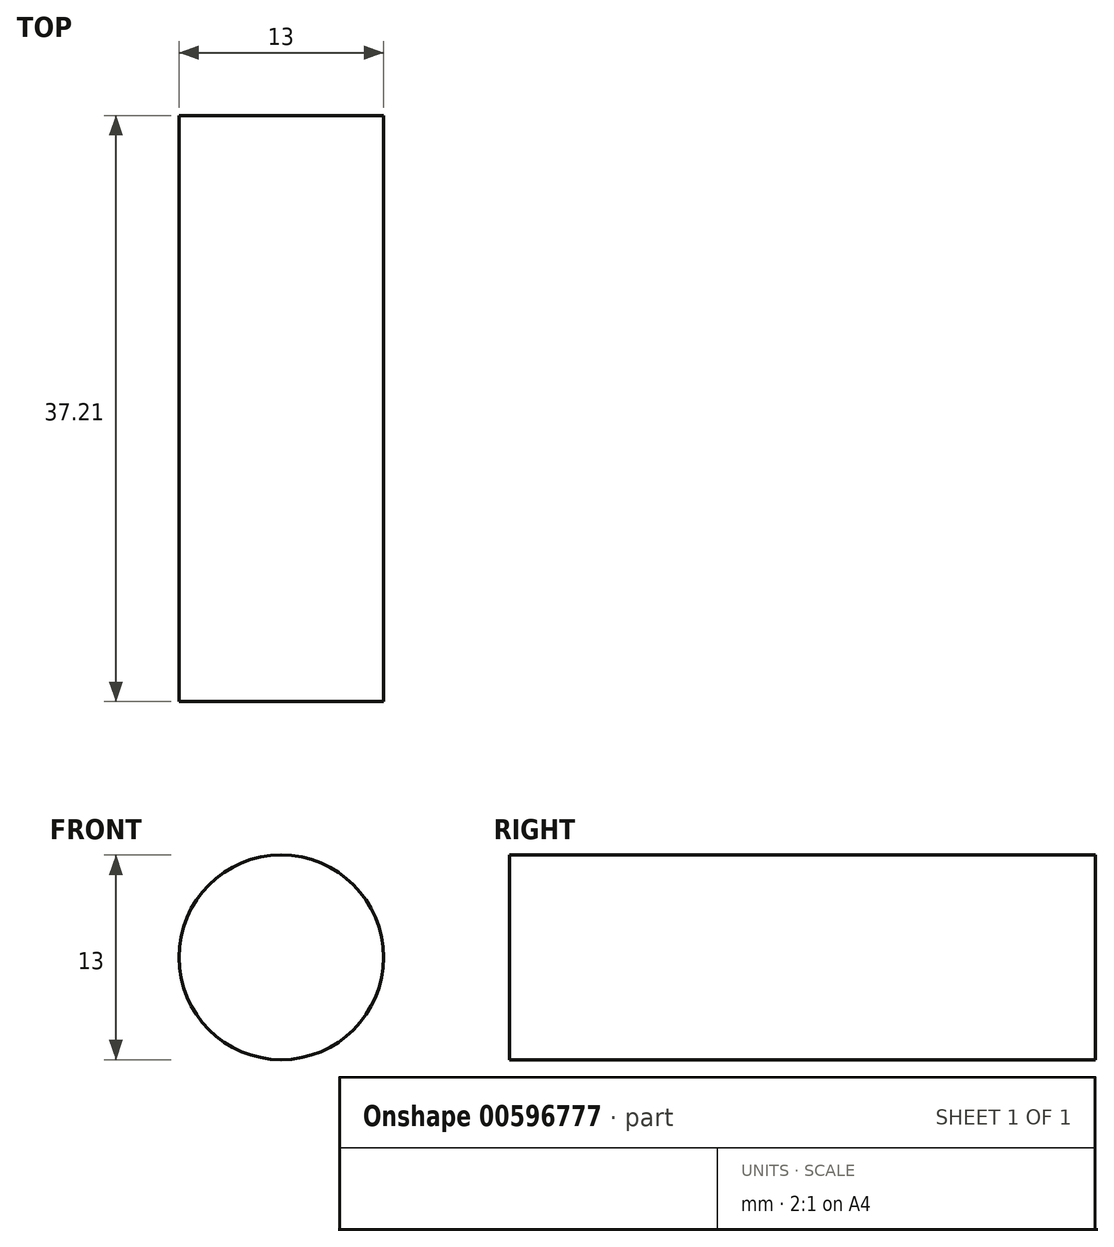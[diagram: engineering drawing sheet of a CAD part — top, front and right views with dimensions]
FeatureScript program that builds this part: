
annotation { "Feature Type Name" : "Feature", "Feature Type Description" : "" }
export const myFeature = defineFeature(function(context is Context, id is Id, definition is map)
    precondition{}
    {
        {
            var Q0;
            Q0=qCreatedBy(makeId("Front.planeOp"),FACE);
            var sketch = newSketch(context, id + "F0", { "sketchPlane" : qUnion([Q0])});
            skCircle(sketch, "E0", {"center": v(0, 0) * mm, "radius": 6.5 * mm});
            skSolve(sketch);
        }
        {
            var Q0;
            Q0 = qSketchRegion(id + "F0", true);
            extrude(context, id + "F1", {"entities" : qUnion([Q0]), "depth" : 37.2 * mm, "offsetDistance" : 25.4 * mm});
        }
    });
